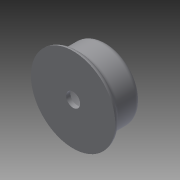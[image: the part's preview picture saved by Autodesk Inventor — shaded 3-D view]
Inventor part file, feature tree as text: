
AUTODESK INVENTOR PART (.ipt)
format: ipt  version: 2014 SP2 (Build 180246200, 246)  size: 164,864 bytes
history: native  units: mm
features: extrude x3, sketch x3, fillet x2
ambient origin geometry x8: Origin, YZ Plane, XZ Plane, XY Plane, X Axis, Y Axis, Z Axis, Center Point
bodies: Solid1 (feature_tree)
feature tree (8):
  extrude  "Extrusion1"  Depth=10.0mm
  fillet  "Fillet1"  Radius=10.0mm
  extrude  "Extrusion2"  Depth=30.0mm
  fillet  "Fillet3"  Radius=2.0mm
  extrude  "Extrusion3"  Depth=0.5mm
  sketch  "Sketch1"  dims[d0=18.5mm d1=24.5mm d2=10.0mm d3=0.0mm]
  sketch  "Sketch2"  dims[d4=2.0mm d6=30.0mm d7=2.0mm d8=0.0mm]
  sketch  "Sketch3"  dims[d9=5.0mm d10=2.0mm d12=7.0mm d13=0.5mm d14=0.0mm]
